# Revit family: RUFO-390-1800-830-Zx
name_source: partatom
category: Leuchten
revit_build: Autodesk Revit 2017 (Build: 20190508_0315(x64)
units: mm (PartAtom-declared; Revit-internal decimal feet)

## family parameters
Basisbauteil = Fläche
Beim Laden mit Abzugskörper schneiden = Ja
Bemaßung runder Anschluss = Durchmesser verwenden
Gemeinsam genutzt = Nein
Lichtquelle = Ja
OmniClass-Nummer = 23.80.70.11
OmniClass-Titel = Luminaries for Internal Lighting
Raumberechnungspunkt = Nein
Teiletyp = Normal

## types (9) — shared parameters
Baugruppenkennzeichen = D5020200
Datei für fotometrisches Netz = RUFO 3901800-840-Z.IES
Emissionsform beim Rendern sichtbar = Nein
Farbfilter = 16777215
Farbtemperaturverschiebung bei Dämpfen der Lampe = <Keine Auswahl>
Hersteller = RIDI Leuchten GmbH
Lampe = LED
Neigungswinkel = 90.00°
Scheinlast = 14 VA
URL = www.ridi.de
Von Kreisdurchmesser aussenden = 370 mm  [stored 1.21391 ft]
brand = RIDI
conformity mark = CE
electrical safety class = 1
height = 85 mm  [stored 0.278871 ft]
ingress protection (IP) code = IP20
length = 370 mm  [stored 1.21391 ft]
nominal frequency = 50-60Hz
nominal voltage = 230
rated input power = 14
voltage type (AC, DC, UC) = AC
width = 370 mm  [stored 1.21391 ft]
zero-valued in all types: Vorgabe-Ansicht

## per-type parameters (varying)
| type | Modell | weight |
| RUFO 390/1800-830 Z | 0420762 | 1.2kg |
| RUFO 390/1800-830 Z-DALI | 0430762 | 1.2kg |
| RUFO 390/1800-830 Z-2K | 0420763 | 1.2kg |
| RUFO 390/1800-830 Z-2K-EDS3 | 0420763//377 | 1.2kg |
| RUFO 390/1800-830 Z-2K-RS | 0420763//396 | 1.2kg |
| RUFO 390/1800-830 Z-2K-RS-EDS3 | 0420763//377396 | 1.2kg |
| RUFO 390/1800-830 Z-EDS3 | 0420762//377 | 1.37kg |
| RUFO 390/1800-830 Z-RS | 0420762//396 | 1.2kg |
| RUFO 390/1800-830 Z-RS-EDS3 | 0420762//377396 | 1.2kg |

note: column(s) folded — value = type name in every type: product name

note: [stored X ft] marks values corroborated as IEEE doubles in the binary element streams (Revit-internal decimal feet)
